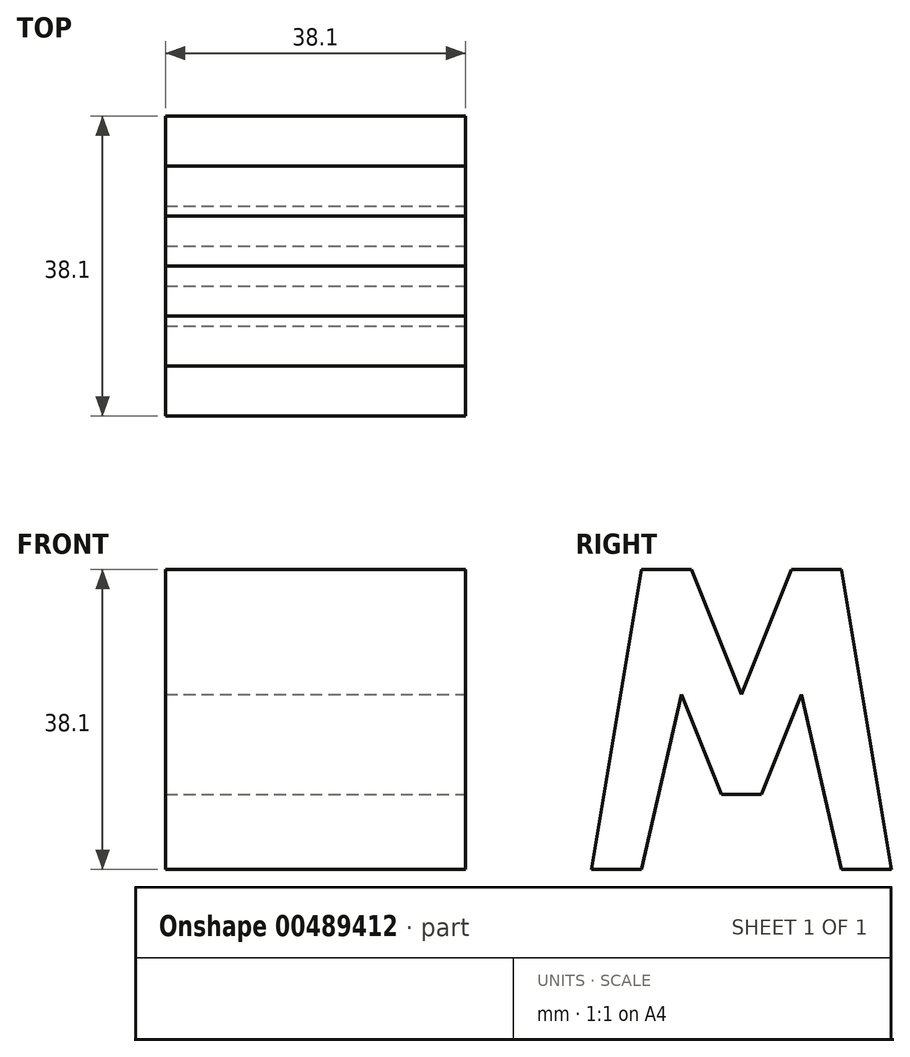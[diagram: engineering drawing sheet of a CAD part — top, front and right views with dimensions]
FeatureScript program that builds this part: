
annotation { "Feature Type Name" : "Feature", "Feature Type Description" : "" }
export const myFeature = defineFeature(function(context is Context, id is Id, definition is map)
    precondition{}
    {
        {
            var Q0;
            Q0=qCreatedBy(makeId("Front.planeOp"),FACE);
            var sketch = newSketch(context, id + "F0", { "sketchPlane" : qUnion([Q0])});
            skLineSegment(sketch, "E0", {"start": v(0, 0) * mm, "end": v(0, 38.1) * mm});
            skLineSegment(sketch, "E1", {"start": v(0, 38.1) * mm, "end": v(38.1, 38.1) * mm});
            skLineSegment(sketch, "E2", {"start": v(38.1, 38.1) * mm, "end": v(38.1, 0) * mm});
            skLineSegment(sketch, "E3", {"start": v(38.1, 0) * mm, "end": v(0, 0) * mm});
            skSolve(sketch);
        }
        {
            var Q0;
            Q0 = qSketchRegion(id + "F0", true);
            extrude(context, id + "F1", {"entities" : qUnion([Q0]), "depth" : 38.1 * mm, "offsetDistance" : 25.4 * mm});
        }
        {
            var Q0;
            Q0=qCreatedBy(makeId("Right.planeOp"),FACE);
            cPlane(context, id + "F2", {"entities" : qUnion([Q0]), "cplaneType" : CPlaneType.OFFSET, "offset" : 38.1 * mm, "width" : 152.4 * mm, "height" : 152.4 * mm});
        }
        {
            var Q0;
            Q0=qCreatedBy(makeId("Top.planeOp"),FACE);
            cPlane(context, id + "F3", {"entities" : qUnion([Q0]), "cplaneType" : CPlaneType.OFFSET, "offset" : 38.1 * mm, "width" : 152.4 * mm, "height" : 152.4 * mm});
        }
        {
            var Q0;
            Q0=qCreatedBy(id+"F2.planeOp",FACE);
            var sketch = newSketch(context, id + "F4", { "sketchPlane" : qUnion([Q0])});
            skLineSegment(sketch, "E4", {"start": v(0, 0) * mm, "end": v(0, 38.1) * mm});
            skLineSegment(sketch, "E5", {"start": v(0, 38.1) * mm, "end": v(-38.1, 38.1) * mm});
            skLineSegment(sketch, "E6", {"start": v(-38.1, 38.1) * mm, "end": v(-38.1, 0) * mm});
            skLineSegment(sketch, "E7", {"start": v(-38.1, 0) * mm, "end": v(0, 0) * mm});
            skLineSegment(sketch, "E8", {"start": v(-38.1, 0) * mm, "end": v(-31.75, 38.1) * mm});
            skLineSegment(sketch, "E9", {"start": v(-25.4, 38.1) * mm, "end": v(-19.05, 22.23) * mm});
            skLineSegment(sketch, "E10", {"start": v(-19.05, 22.23) * mm, "end": v(-12.7, 38.1) * mm});
            skLineSegment(sketch, "E11", {"start": v(-6.35, 38.1) * mm, "end": v(0, 0) * mm});
            skLineSegment(sketch, "E12", {"start": v(-31.75, 0) * mm, "end": v(-26.67, 22.23) * mm});
            skLineSegment(sketch, "E13", {"start": v(-26.67, 22.23) * mm, "end": v(-21.59, 9.53) * mm});
            skLineSegment(sketch, "E14", {"start": v(-21.59, 9.53) * mm, "end": v(-16.5, 9.53) * mm});
            skLineSegment(sketch, "E15", {"start": v(-16.5, 9.53) * mm, "end": v(-11.43, 22.23) * mm});
            skLineSegment(sketch, "E16", {"start": v(-11.43, 22.23) * mm, "end": v(-6.35, 0) * mm});
            skSolve(sketch);
        }
        {
            var Q0;
            {var subQ0=sQuery(id+"F4.wireOp",EDGE,"E6");Q0=makeQuery(id+"F4.imprint","IMPRINT",FACE,{"disambiguationData":[TD([[makeQuery(id+"F4.imprint","IMPRINT",EDGE,{"derivedFrom":subQ0}),1.0]])]});}
            var Q1;
            {var subQ0=sQuery(id+"F4.wireOp",EDGE,"E9");Q1=makeQuery(id+"F4.imprint","IMPRINT",FACE,{"disambiguationData":[TD([[makeQuery(id+"F4.imprint","IMPRINT",EDGE,{"derivedFrom":subQ0}),1.0]])]});}
            var Q2;
            {var subQ0=sQuery(id+"F4.wireOp",EDGE,"E4");Q2=makeQuery(id+"F4.imprint","IMPRINT",FACE,{"disambiguationData":[TD([[makeQuery(id+"F4.imprint","IMPRINT",EDGE,{"derivedFrom":subQ0}),1.0]])]});}
            var Q3;
            {var subQ0=sQuery(id+"F4.wireOp",EDGE,"E12");Q3=makeQuery(id+"F4.imprint","IMPRINT",FACE,{"disambiguationData":[TD([[makeQuery(id+"F4.imprint","IMPRINT",EDGE,{"derivedFrom":subQ0}),-1.0]])]});}
            extrude(context, id + "F5", {"entities" : qUnion([Q0, Q1, Q2, Q3]), "operationType" : NewBodyOperationType.REMOVE, "oppositeDirection" : true, "depth" : 38.1 * mm, "offsetDistance" : 25.4 * mm});
        }
    });
